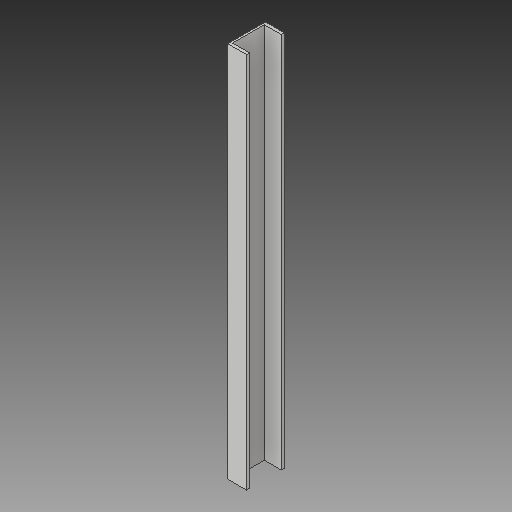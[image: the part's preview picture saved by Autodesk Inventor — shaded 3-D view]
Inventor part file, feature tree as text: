
AUTODESK INVENTOR PART (.ipt)
format: ipt  version: 2019 (Build 230136000, 136)  size: 87,040 bytes
history: native  units: in
note: dims shown in document units (in); Inventor stores cm internally (conversion verified against a paired STEP export)
features: other x3, sketch x1
ambient origin geometry x8: Origin, YZ Plane, XZ Plane, XY Plane, X Axis, Y Axis, Z Axis, Center Point
bodies: Solid1 (feature_tree)
feature tree (4):
  other  "Channel1_MIR_MIR2.ipt"
  other  "Solid1::Channel1_MIR_MIR2.ipt"
  other  "TaggingFeature1"
  sketch  "Sketch1"  dims[d0=0.3937in]
